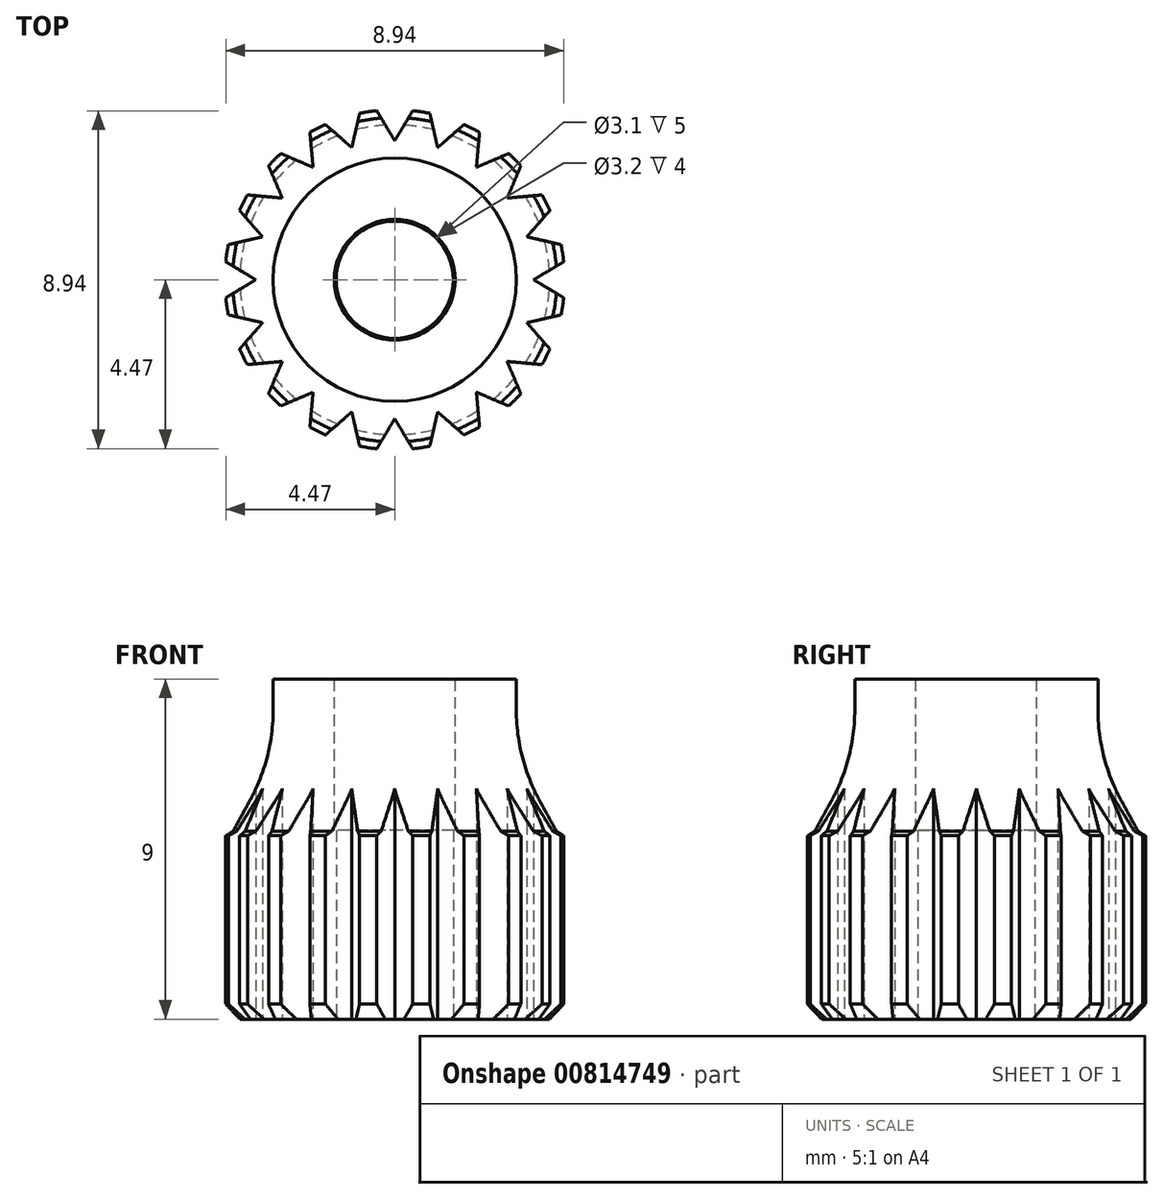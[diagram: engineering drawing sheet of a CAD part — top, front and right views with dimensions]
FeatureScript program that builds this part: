
annotation { "Feature Type Name" : "Feature", "Feature Type Description" : "" }
export const myFeature = defineFeature(function(context is Context, id is Id, definition is map)
    precondition{}
    {
        {
            var Q0;
            Q0=qCreatedBy(makeId("Top.planeOp"),FACE);
            var sketch = newSketch(context, id + "F0", { "sketchPlane" : qUnion([Q0])});
            skCircle(sketch, "E0", {"center": v(0, 0) * mm, "radius": 1.55 * mm});
            skCircle(sketch, "E1", {"center": v(0, 0) * mm, "radius": 4.5 * mm});
            skSolve(sketch);
        }
        {
            var Q0;
            Q0=makeQuery(id+"F0.imprint","IMPRINT",FACE,{"disambiguationData":[TD([[makeQuery(id+"F0.imprint","IMPRINT",EDGE,{"derivedFrom":sQuery(id+"F0.wireOp",EDGE,"E0")}),-1.0]])]});
            extrude(context, id + "F1", {"entities" : qUnion([Q0]), "depth" : 9 * mm, "offsetDistance" : 25 * mm});
        }
        {
            var Q0;
            Q0=qCreatedBy(makeId("Right.planeOp"),FACE);
            var sketch = newSketch(context, id + "F2", { "sketchPlane" : qUnion([Q0])});
            skLineSegment(sketch, "E2", {"start": v(-3.22, 10.3) * mm, "end": v(-3.22, 6.88) * mm});
            skLineSegment(sketch, "E3", {"start": v(-3.22, 6.88) * mm, "end": v(-4.4, 4.77) * mm});
            skLineSegment(sketch, "E4", {"start": v(-4.4, 4.77) * mm, "end": v(-4.76, 4.77) * mm});
            skLineSegment(sketch, "E5", {"start": v(-4.76, 4.77) * mm, "end": v(-4.76, 10.25) * mm});
            skLineSegment(sketch, "E6", {"start": v(-4.76, 10.25) * mm, "end": v(-3.22, 10.3) * mm});
            skSolve(sketch);
        }
        {
            var Q0;
            Q0 = qSketchRegion(id + "F2", true);
            var Q1;
            Q1=makeQuery(id+"F1.opExtrude","CAP_EDGE",EDGE,{"disambiguationData":[OSD([sQuery(id+"F0.wireOp",EDGE,"E0")])],"isStart":false});
            revolve(context, id + "F3", {"surfaceOperationType" : NewSurfaceOperationType.NEW, "entities" : qUnion([Q0]), "axis" : qUnion([Q1]), "revolveType" : RevolveType.FULL});
        }
        {
            var Q0;
            Q0=makeQuery(id+"F3.opRevolve","SWEPT_BODY",BODY,{"disambiguationData":[OSD([sQuery(id+"F2.wireOp",EDGE,"E2"),sQuery(id+"F2.wireOp",EDGE,"E3"),sQuery(id+"F2.wireOp",EDGE,"E4"),sQuery(id+"F2.wireOp",EDGE,"E5"),sQuery(id+"F2.wireOp",EDGE,"E6")])]});
            var Q1;
            Q1=makeQuery(id+"F1.opExtrude","SWEPT_BODY",BODY,{"disambiguationData":[OSD([sQuery(id+"F0.wireOp",EDGE,"E0"),sQuery(id+"F0.wireOp",EDGE,"E1")])]});
            booleanBodies(context, id + "F4", {"operationType" : BooleanOperationType.SUBTRACTION, "tools" : qUnion([Q0]), "targets" : qUnion([Q1])});
        }
        {
            var Q0;
            {var subQ0=sQuery(id+"F0.wireOp",EDGE,"E1");var subQ1=makeQuery(id+"FQQbT9eo0qdUzTb_1.opSweep","CAP_FACE",FACE,{"disambiguationData":[OSD([subQ0,dummyQuery(id+"FF1MUGfiOZVIYez_1.opHelix",VERTEX,0.0),sQuery(id+"FiRf2puYs6quxog_1.wireOp",EDGE,"J0xlJ2EH-lt4b-WaQl-g26T-4OqvbinfoNN3"),sQuery(id+"FiRf2puYs6quxog_1.wireOp",EDGE,"0tNh7jCX-wTse-oJeZ-rxhu-BOIblvZp0hQE")])],"isStart":true});Q0=makeQuery(id+"FpPIVENxbjl4PfN_3.opBoolean","MERGE",FACE,{"derivedFrom":[makeQuery(id+"F1.opExtrude","CAP_FACE",FACE,{"disambiguationData":[OSD([sQuery(id+"F0.wireOp",EDGE,"E0"),subQ0])],"isStart":false}),subQ1,makeQuery(id+"FoVqAVhd8NQIFPW_3.opPattern","COPY",FACE,{"derivedFrom":subQ1,"instanceName":"1"}),makeQuery(id+"FoVqAVhd8NQIFPW_3.opPattern","COPY",FACE,{"derivedFrom":subQ1,"instanceName":"2"}),makeQuery(id+"FoVqAVhd8NQIFPW_3.opPattern","COPY",FACE,{"derivedFrom":subQ1,"instanceName":"3"}),makeQuery(id+"FoVqAVhd8NQIFPW_3.opPattern","COPY",FACE,{"derivedFrom":subQ1,"instanceName":"4"}),makeQuery(id+"FoVqAVhd8NQIFPW_3.opPattern","COPY",FACE,{"derivedFrom":subQ1,"instanceName":"5"}),makeQuery(id+"FoVqAVhd8NQIFPW_3.opPattern","COPY",FACE,{"derivedFrom":subQ1,"instanceName":"6"}),makeQuery(id+"FoVqAVhd8NQIFPW_3.opPattern","COPY",FACE,{"derivedFrom":subQ1,"instanceName":"7"}),makeQuery(id+"FoVqAVhd8NQIFPW_3.opPattern","COPY",FACE,{"derivedFrom":subQ1,"instanceName":"8"}),makeQuery(id+"FoVqAVhd8NQIFPW_3.opPattern","COPY",FACE,{"derivedFrom":subQ1,"instanceName":"9"}),makeQuery(id+"FoVqAVhd8NQIFPW_3.opPattern","COPY",FACE,{"derivedFrom":subQ1,"instanceName":"10"}),makeQuery(id+"FoVqAVhd8NQIFPW_3.opPattern","COPY",FACE,{"derivedFrom":subQ1,"instanceName":"11"}),makeQuery(id+"FoVqAVhd8NQIFPW_3.opPattern","COPY",FACE,{"derivedFrom":subQ1,"instanceName":"12"}),makeQuery(id+"FoVqAVhd8NQIFPW_3.opPattern","COPY",FACE,{"derivedFrom":subQ1,"instanceName":"13"}),makeQuery(id+"FoVqAVhd8NQIFPW_3.opPattern","COPY",FACE,{"derivedFrom":subQ1,"instanceName":"14"}),makeQuery(id+"FoVqAVhd8NQIFPW_3.opPattern","COPY",FACE,{"derivedFrom":subQ1,"instanceName":"15"}),makeQuery(id+"FoVqAVhd8NQIFPW_3.opPattern","COPY",FACE,{"derivedFrom":subQ1,"instanceName":"16"}),makeQuery(id+"FoVqAVhd8NQIFPW_3.opPattern","COPY",FACE,{"derivedFrom":subQ1,"instanceName":"17"}),makeQuery(id+"FoVqAVhd8NQIFPW_3.opPattern","COPY",FACE,{"derivedFrom":subQ1,"instanceName":"18"}),makeQuery(id+"FoVqAVhd8NQIFPW_3.opPattern","COPY",FACE,{"derivedFrom":subQ1,"instanceName":"19"})]});}
            var sketch = newSketch(context, id + "F5", { "sketchPlane" : qUnion([Q0])});
            skCircle(sketch, "E7", {"center": v(0, 0) * mm, "radius": 1.6 * mm});
            skSolve(sketch);
        }
        {
            var Q0;
            Q0 = qSketchRegion(id + "F5", true);
            extrude(context, id + "F6", {"entities" : qUnion([Q0]), "operationType" : NewBodyOperationType.REMOVE, "oppositeDirection" : true, "depth" : 4 * mm, "offsetDistance" : 25 * mm});
        }
        {
            var Q0;
            Q0=makeQuery(id+"F4.opBoolean","COPY",EDGE,{"derivedFrom":makeQuery(id+"F3.opRevolve","SWEPT_EDGE",EDGE,{"disambiguationData":[OSD([sQuery(id+"F2.wireOp",EDGE,"E3"),sQuery(id+"F2.wireOp",EDGE,"E4")])]})});
            var Q1;
            Q1=makeQuery(id+"F1.opExtrude","CAP_EDGE",EDGE,{"disambiguationData":[OSD([sQuery(id+"F0.wireOp",EDGE,"E1")])],"isStart":true});
            var Q2;
            Q2=makeQuery(id+"F1.opExtrude","CAP_EDGE",EDGE,{"disambiguationData":[OSD([sQuery(id+"F0.wireOp",EDGE,"E0")])],"isStart":false});
            var Q3;
            Q3=makeQuery(id+"F6.boolean.opBoolean","COPY",EDGE,{"derivedFrom":makeQuery(id+"F6.opExtrude","CAP_EDGE",EDGE,{"disambiguationData":[OSD([sQuery(id+"F5.wireOp",EDGE,"E7")])],"isStart":true})});
            chamfer(context, id + "F7", {"entities" : qUnion([Q0, Q1, Q2, Q3]), "width" : 0.4 * mm, "tangentPropagation" : true});
        }
        {
            var Q0;
            Q0=makeQuery(id+"F4.opBoolean","COPY",EDGE,{"derivedFrom":makeQuery(id+"F3.opRevolve","SWEPT_EDGE",EDGE,{"disambiguationData":[OSD([sQuery(id+"F2.wireOp",EDGE,"E2"),sQuery(id+"F2.wireOp",EDGE,"E3")])]})});
            fillet(context, id + "F8", {"entities" : qUnion([Q0]), "radius" : 5 * mm, "tangentPropagation" : true, "allowEdgeOverflow" : false});
        }
        {
            var Q0;
            Q0=qCreatedBy(makeId("Top.planeOp"),FACE);
            var sketch = newSketch(context, id + "F9", { "sketchPlane" : qUnion([Q0])});
            skLineSegment(sketch, "E8", {"start": v(-0.64, -4.75) * mm, "end": v(0, -3.68) * mm});
            skLineSegment(sketch, "E9", {"start": v(0, -3.68) * mm, "end": v(0.64, -4.75) * mm});
            skLineSegment(sketch, "E10", {"start": v(0.64, -4.75) * mm, "end": v(-0.64, -4.75) * mm});
            skSolve(sketch);
        }
        {
            var Q0;
            Q0=makeQuery(id+"F9.imprint","IMPRINT",FACE,{"disambiguationData":[TD([[makeQuery(id+"F9.imprint","IMPRINT",EDGE,{"derivedFrom":sQuery(id+"F9.wireOp",EDGE,"E8")}),-1.0]])]});
            extrude(context, id + "F10", {"entities" : qUnion([Q0]), "depth" : 25 * mm, "offsetDistance" : 25 * mm});
        }
        {
            var Q0;
            Q0=makeQuery(id+"F10.opExtrude","SWEPT_BODY",BODY,{"disambiguationData":[OSD([sQuery(id+"F9.wireOp",EDGE,"E8"),sQuery(id+"F9.wireOp",EDGE,"E9"),sQuery(id+"F9.wireOp",EDGE,"E10")])]});
            var Q1;
            {var subQ0=sQuery(id+"F0.wireOp",EDGE,"E1");Q1=makeQuery(id+"F7.opChamfer","BLEND_EDGE",EDGE,{"blendedFrom":[makeQuery(id+"F1.opExtrude","CAP_EDGE",EDGE,{"disambiguationData":[OSD([subQ0])],"isStart":true}),makeQuery(id+"F1.opExtrude","SWEPT_FACE",FACE,{"disambiguationData":[OSD([subQ0])]})],"blendedInto":[makeQuery(id+"F1.opExtrude","SWEPT_FACE",FACE,{"disambiguationData":[OSD([subQ0])]})]});}
            circularPattern(context, id + "F11", {"entities" : qUnion([Q0]), "axis" : qUnion([Q1]), "angle" : 360 * degree, "instanceCount" : 20, "equalSpace" : true});
        }
        {
            var Q0;
            Q0=makeQuery(id+"F10.opExtrude","SWEPT_BODY",BODY,{"disambiguationData":[OSD([sQuery(id+"F9.wireOp",EDGE,"E8"),sQuery(id+"F9.wireOp",EDGE,"E9"),sQuery(id+"F9.wireOp",EDGE,"E10")])]});
            var Q1;
            Q1=makeQuery(id+"F11.opPattern","COPY",BODY,{"derivedFrom":makeQuery(id+"F10.opExtrude","SWEPT_BODY",BODY,{"disambiguationData":[OSD([sQuery(id+"F9.wireOp",EDGE,"E8"),sQuery(id+"F9.wireOp",EDGE,"E9"),sQuery(id+"F9.wireOp",EDGE,"E10")])]}),"instanceName":"1"});
            var Q2;
            Q2=makeQuery(id+"F11.opPattern","COPY",BODY,{"derivedFrom":makeQuery(id+"F10.opExtrude","SWEPT_BODY",BODY,{"disambiguationData":[OSD([sQuery(id+"F9.wireOp",EDGE,"E8"),sQuery(id+"F9.wireOp",EDGE,"E9"),sQuery(id+"F9.wireOp",EDGE,"E10")])]}),"instanceName":"2"});
            var Q3;
            Q3=makeQuery(id+"F11.opPattern","COPY",BODY,{"derivedFrom":makeQuery(id+"F10.opExtrude","SWEPT_BODY",BODY,{"disambiguationData":[OSD([sQuery(id+"F9.wireOp",EDGE,"E8"),sQuery(id+"F9.wireOp",EDGE,"E9"),sQuery(id+"F9.wireOp",EDGE,"E10")])]}),"instanceName":"3"});
            var Q4;
            Q4=makeQuery(id+"F11.opPattern","COPY",BODY,{"derivedFrom":makeQuery(id+"F10.opExtrude","SWEPT_BODY",BODY,{"disambiguationData":[OSD([sQuery(id+"F9.wireOp",EDGE,"E8"),sQuery(id+"F9.wireOp",EDGE,"E9"),sQuery(id+"F9.wireOp",EDGE,"E10")])]}),"instanceName":"4"});
            var Q5;
            Q5=makeQuery(id+"F11.opPattern","COPY",BODY,{"derivedFrom":makeQuery(id+"F10.opExtrude","SWEPT_BODY",BODY,{"disambiguationData":[OSD([sQuery(id+"F9.wireOp",EDGE,"E8"),sQuery(id+"F9.wireOp",EDGE,"E9"),sQuery(id+"F9.wireOp",EDGE,"E10")])]}),"instanceName":"5"});
            var Q6;
            Q6=makeQuery(id+"F11.opPattern","COPY",BODY,{"derivedFrom":makeQuery(id+"F10.opExtrude","SWEPT_BODY",BODY,{"disambiguationData":[OSD([sQuery(id+"F9.wireOp",EDGE,"E8"),sQuery(id+"F9.wireOp",EDGE,"E9"),sQuery(id+"F9.wireOp",EDGE,"E10")])]}),"instanceName":"6"});
            var Q7;
            Q7=makeQuery(id+"F11.opPattern","COPY",BODY,{"derivedFrom":makeQuery(id+"F10.opExtrude","SWEPT_BODY",BODY,{"disambiguationData":[OSD([sQuery(id+"F9.wireOp",EDGE,"E8"),sQuery(id+"F9.wireOp",EDGE,"E9"),sQuery(id+"F9.wireOp",EDGE,"E10")])]}),"instanceName":"7"});
            var Q8;
            Q8=makeQuery(id+"F11.opPattern","COPY",BODY,{"derivedFrom":makeQuery(id+"F10.opExtrude","SWEPT_BODY",BODY,{"disambiguationData":[OSD([sQuery(id+"F9.wireOp",EDGE,"E8"),sQuery(id+"F9.wireOp",EDGE,"E9"),sQuery(id+"F9.wireOp",EDGE,"E10")])]}),"instanceName":"8"});
            var Q9;
            Q9=makeQuery(id+"F11.opPattern","COPY",BODY,{"derivedFrom":makeQuery(id+"F10.opExtrude","SWEPT_BODY",BODY,{"disambiguationData":[OSD([sQuery(id+"F9.wireOp",EDGE,"E8"),sQuery(id+"F9.wireOp",EDGE,"E9"),sQuery(id+"F9.wireOp",EDGE,"E10")])]}),"instanceName":"9"});
            var Q10;
            Q10=makeQuery(id+"F11.opPattern","COPY",BODY,{"derivedFrom":makeQuery(id+"F10.opExtrude","SWEPT_BODY",BODY,{"disambiguationData":[OSD([sQuery(id+"F9.wireOp",EDGE,"E8"),sQuery(id+"F9.wireOp",EDGE,"E9"),sQuery(id+"F9.wireOp",EDGE,"E10")])]}),"instanceName":"10"});
            var Q11;
            Q11=makeQuery(id+"F11.opPattern","COPY",BODY,{"derivedFrom":makeQuery(id+"F10.opExtrude","SWEPT_BODY",BODY,{"disambiguationData":[OSD([sQuery(id+"F9.wireOp",EDGE,"E8"),sQuery(id+"F9.wireOp",EDGE,"E9"),sQuery(id+"F9.wireOp",EDGE,"E10")])]}),"instanceName":"11"});
            var Q12;
            Q12=makeQuery(id+"F11.opPattern","COPY",BODY,{"derivedFrom":makeQuery(id+"F10.opExtrude","SWEPT_BODY",BODY,{"disambiguationData":[OSD([sQuery(id+"F9.wireOp",EDGE,"E8"),sQuery(id+"F9.wireOp",EDGE,"E9"),sQuery(id+"F9.wireOp",EDGE,"E10")])]}),"instanceName":"12"});
            var Q13;
            Q13=makeQuery(id+"F11.opPattern","COPY",BODY,{"derivedFrom":makeQuery(id+"F10.opExtrude","SWEPT_BODY",BODY,{"disambiguationData":[OSD([sQuery(id+"F9.wireOp",EDGE,"E8"),sQuery(id+"F9.wireOp",EDGE,"E9"),sQuery(id+"F9.wireOp",EDGE,"E10")])]}),"instanceName":"13"});
            var Q14;
            Q14=makeQuery(id+"F11.opPattern","COPY",BODY,{"derivedFrom":makeQuery(id+"F10.opExtrude","SWEPT_BODY",BODY,{"disambiguationData":[OSD([sQuery(id+"F9.wireOp",EDGE,"E8"),sQuery(id+"F9.wireOp",EDGE,"E9"),sQuery(id+"F9.wireOp",EDGE,"E10")])]}),"instanceName":"14"});
            var Q15;
            Q15=makeQuery(id+"F11.opPattern","COPY",BODY,{"derivedFrom":makeQuery(id+"F10.opExtrude","SWEPT_BODY",BODY,{"disambiguationData":[OSD([sQuery(id+"F9.wireOp",EDGE,"E8"),sQuery(id+"F9.wireOp",EDGE,"E9"),sQuery(id+"F9.wireOp",EDGE,"E10")])]}),"instanceName":"15"});
            var Q16;
            Q16=makeQuery(id+"F11.opPattern","COPY",BODY,{"derivedFrom":makeQuery(id+"F10.opExtrude","SWEPT_BODY",BODY,{"disambiguationData":[OSD([sQuery(id+"F9.wireOp",EDGE,"E8"),sQuery(id+"F9.wireOp",EDGE,"E9"),sQuery(id+"F9.wireOp",EDGE,"E10")])]}),"instanceName":"16"});
            var Q17;
            Q17=makeQuery(id+"F11.opPattern","COPY",BODY,{"derivedFrom":makeQuery(id+"F10.opExtrude","SWEPT_BODY",BODY,{"disambiguationData":[OSD([sQuery(id+"F9.wireOp",EDGE,"E8"),sQuery(id+"F9.wireOp",EDGE,"E9"),sQuery(id+"F9.wireOp",EDGE,"E10")])]}),"instanceName":"17"});
            var Q18;
            Q18=makeQuery(id+"F11.opPattern","COPY",BODY,{"derivedFrom":makeQuery(id+"F10.opExtrude","SWEPT_BODY",BODY,{"disambiguationData":[OSD([sQuery(id+"F9.wireOp",EDGE,"E8"),sQuery(id+"F9.wireOp",EDGE,"E9"),sQuery(id+"F9.wireOp",EDGE,"E10")])]}),"instanceName":"18"});
            var Q19;
            Q19=makeQuery(id+"F11.opPattern","COPY",BODY,{"derivedFrom":makeQuery(id+"F10.opExtrude","SWEPT_BODY",BODY,{"disambiguationData":[OSD([sQuery(id+"F9.wireOp",EDGE,"E8"),sQuery(id+"F9.wireOp",EDGE,"E9"),sQuery(id+"F9.wireOp",EDGE,"E10")])]}),"instanceName":"19"});
            var Q20;
            Q20=makeQuery(id+"F1.opExtrude","SWEPT_BODY",BODY,{"disambiguationData":[OSD([sQuery(id+"F0.wireOp",EDGE,"E0"),sQuery(id+"F0.wireOp",EDGE,"E1")])]});
            booleanBodies(context, id + "F12", {"operationType" : BooleanOperationType.SUBTRACTION, "tools" : qUnion([Q0, Q1, Q2, Q3, Q4, Q5, Q6, Q7, Q8, Q9, Q10, Q11, Q12, Q13, Q14, Q15, Q16, Q17, Q18, Q19]), "targets" : qUnion([Q20])});
        }
    });
